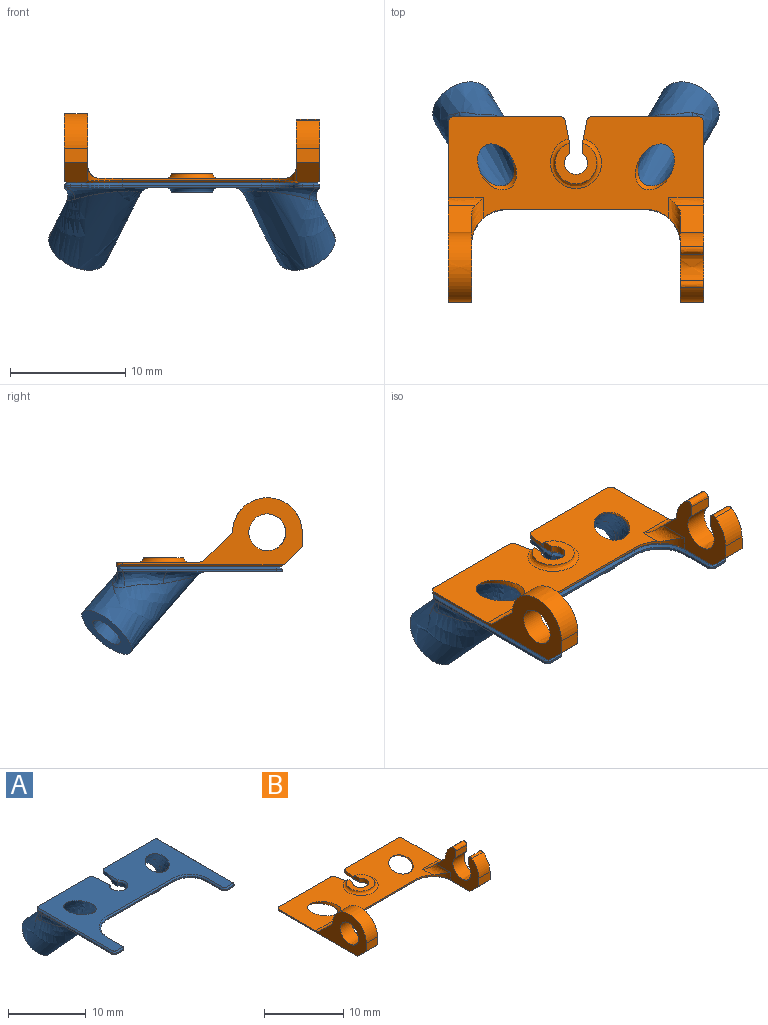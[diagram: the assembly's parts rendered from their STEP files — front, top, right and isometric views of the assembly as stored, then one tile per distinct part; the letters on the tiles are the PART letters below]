
ASSEMBLY  parts=2 mates=1
PART A: 60 faces, bbox 27.5x19.2x12.5 mm
  f0: plane 13.43x0.32mm, normal (1,0,0), area 2.7mm2, adj f16,f24,f33,f41,f59
  f1: plane 1.01x0.2mm, normal (0,-1,0), area 0.2mm2, adj f16,f24,f25,f57
  f2: plane 2.76x0.2mm, normal (-1,0,0), area 0.6mm2, adj f3,f16,f25,f55
  f3: cylinder r=3.01mm len=3.02mm, axis (0,0,1), area 0.9mm2, adj f2,f4,f16,f54
  f4: plane 12.06x0.2mm, normal (0,-1,0), area 2.4mm2, adj f3,f5,f16,f53
  f5: cylinder r=3.01mm len=3.02mm, axis (0,0,1), area 0.9mm2, adj f4,f6,f16,f52
  f6: plane 2.76x0.2mm, normal (1,0,0), area 0.6mm2, adj f5,f16,f26,f51
  f7: plane 1.01x0.2mm, normal (0,-1,0), area 0.2mm2, adj f16,f26,f27,f49
  f8: plane 13.43x0.33mm, normal (-1,0,0), area 2.7mm2, adj f16,f27,f28,f34,f47
  f9: plane 9.61x0.88mm, normal (0,1,0), area 3.7mm2, adj f16,f17,f28,f29,f37
  f10: plane 1.75x0.49mm, normal (0.98,0.19,0), area 0.6mm2, adj f16,f17,f29,f30,f43,f44
  f11: plane 0.98x0.63mm, normal (1,0,0), area 0.6mm2, adj f12,f30,f42,f43,f44
  f12: cylinder r=1.01mm len=2.01mm, axis (0,0,1), area 3.1mm2, adj f11,f13,f42,f45
  f13: plane 0.98x0.63mm, normal (-1,0,0), area 0.6mm2, adj f12,f31,f42,f43,f46
  f14: plane 1.75x0.49mm, normal (-0.98,0.19,0), area 0.6mm2, adj f16,f17,f31,f32,f43,f46
  f15: plane 9.6x0.87mm, normal (0,1,0), area 3.7mm2, adj f16,f17,f32,f33,f38
  f16: plane 22.29x14.5mm, normal (0,0,-1), area 90.3mm2, adj f0,f1,f2,f3,f4,f5,f6,f7
  f17: plane 21.71x14.11mm, normal (0,0,1), area 165mm2, adj f9,f10,f14,f15,f20,f23,f28,f29
  f18: plane 7.73x6.93mm, normal (0.35,0.61,-0.71), area 15.9mm2, adj f19,f20
  f19: extruded ~10.68x10.27mm, area 107.2mm2, adj f18,f38,f39,f40,f41
  f20: extruded ~8.84x8.23mm, area 76mm2, adj f17,f18
  f21: plane 7.73x6.93mm, normal (-0.35,0.61,-0.71), area 16.1mm2, adj f22,f23
  f22: extruded ~10.68x10.27mm, area 107.2mm2, adj f21,f34,f35,f36,f37
  f23: extruded ~8.84x8.23mm, area 76mm2, adj f17,f21
  f24: cylinder r=0.5mm len=0.5mm, axis (0,0,-1), area 0.2mm2, adj f0,f1,f16,f58
  f25: cylinder r=0.5mm len=0.5mm, axis (0,0,1), area 0.2mm2, adj f1,f2,f16,f56
  f26: cylinder r=0.5mm len=0.5mm, axis (0,0,-1), area 0.2mm2, adj f6,f7,f16,f50
  f27: cylinder r=0.5mm len=0.5mm, axis (0,0,1), area 0.2mm2, adj f7,f8,f16,f48
  f28: cylinder r=0.5mm len=0.5mm, axis (0,0,1), area 0.3mm2, adj f8,f9,f17,f36,f47
  f29: cylinder r=0.5mm len=0.49mm, axis (0,0,-1), area 0.3mm2, adj f9,f10,f16,f17
  f30: cylinder r=0.5mm len=0.4mm, axis (0,0,1), area 0mm2, adj f10,f11,f43,f44
  f31: cylinder r=0.5mm len=0.4mm, axis (0,0,1), area 0mm2, adj f13,f14,f43,f46
  f32: cylinder r=0.5mm len=0.49mm, axis (0,0,1), area 0.3mm2, adj f14,f15,f16,f17
  f33: cylinder r=0.5mm len=0.5mm, axis (0,0,-1), area 0.3mm2, adj f0,f15,f17,f40,f59
  f34: bspline ~3.99x1.35mm, area 4.7mm2, adj f8,f22,f35,f36
  f35: bspline ~7.75x7.5mm, area 16.4mm2, adj f16,f22,f34,f37
  f36: bspline ~1.43x1.06mm, area 1.4mm2, adj f22,f28,f34,f37
  f37: bspline ~5.39x1.22mm, area 3.9mm2, adj f9,f22,f35,f36
  f38: bspline ~5.39x1.22mm, area 3.9mm2, adj f15,f19,f39,f40
  f39: bspline ~7.75x7.5mm, area 16.4mm2, adj f16,f19,f38,f41
  f40: bspline ~1.43x1.06mm, area 1.4mm2, adj f19,f33,f38,f41
  f41: bspline ~3.99x1.35mm, area 4.7mm2, adj f0,f19,f39,f40
  f42: plane 3.62x3.52mm, normal (0,0,-1), area 6.1mm2, adj f11,f12,f13,f43
  f43: bspline ~4.39x4.26mm, area 7mm2, adj f10,f11,f13,f14,f16,f30,f31,f42
  f44: plane 2.03x0.21mm, normal (0.71,0,0.71), area 0.4mm2, adj f10,f11,f17,f30,f45
  f45: cone r=1.01mm half-angle=45deg, axis (0,0,1), area 1.6mm2, adj f12,f17,f44,f46
  f46: plane 2.03x0.21mm, normal (-0.71,0,0.71), area 0.4mm2, adj f13,f14,f17,f31,f45
  f47: plane 13.8x0.29mm, normal (-0.71,0,0.71), area 3.8mm2, adj f8,f17,f28,f48
  f48: cone r=0.3mm half-angle=45deg, axis (0,0,-1), area 0.2mm2, adj f17,f27,f47,f49
  f49: plane 1.01x0.2mm, normal (0,-0.71,0.71), area 0.3mm2, adj f7,f17,f48,f50
  f50: cone r=0.3mm half-angle=45deg, axis (0,0,-1), area 0.2mm2, adj f17,f26,f49,f51
  f51: plane 2.76x0.2mm, normal (0.71,0,0.71), area 0.8mm2, adj f6,f17,f50,f52
  f52: cone r=3.01mm half-angle=45deg, axis (0,0,1), area 1.4mm2, adj f5,f17,f51,f53
  f53: plane 12.06x0.2mm, normal (0,-0.71,0.71), area 3.4mm2, adj f4,f17,f52,f54
  f54: cone r=3.01mm half-angle=45deg, axis (0,0,1), area 1.4mm2, adj f3,f17,f53,f55
  f55: plane 2.76x0.2mm, normal (-0.71,0,0.71), area 0.8mm2, adj f2,f17,f54,f56
  f56: cone r=0.3mm half-angle=45deg, axis (0,0,-1), area 0.2mm2, adj f17,f25,f55,f57
  f57: plane 1.01x0.2mm, normal (0,-0.71,0.71), area 0.3mm2, adj f1,f17,f56,f58
  f58: cone r=0.3mm half-angle=45deg, axis (0,0,-1), area 0.2mm2, adj f17,f24,f57,f59
  f59: plane 13.8x0.29mm, normal (0.71,0,0.71), area 3.8mm2, adj f0,f17,f33,f58
PART B: 55 faces, bbox 23.8x17.8x10.7 mm
  f0: plane 22.11x8.81mm, normal (0,0,1), area 133.7mm2, adj f1,f5,f9,f10,f11,f12,f13,f29
  f1: plane 16.15x5.92mm, normal (1,0,0), area 23.6mm2, adj f0,f3,f4,f21,f22,f23,f24,f25
  f2: plane 8.21x5.92mm, normal (-1,0,0), area 18.3mm2, adj f3,f4,f21,f22,f23,f24,f25,f26
  f3: extruded ~2.42x2.01mm, area 5.7mm2, adj f1,f2,f21,f27
  f4: extruded ~3.21x2.73mm, area 15.2mm2, adj f1,f2,f25,f26
  f5: plane 12.06x0.2mm, normal (0,-1,0), area 2.4mm2, adj f0,f29,f30,f52
  f6: plane 0.98x0.63mm, normal (-1,0,0), area 0.6mm2, adj f7,f42,f43,f44,f45
  f7: cylinder r=1.01mm len=2.01mm, axis (0,0,-1), area 3.1mm2, adj f6,f8,f43,f46
  f8: plane 0.98x0.63mm, normal (1,0,0), area 0.6mm2, adj f7,f37,f43,f44,f47
  f9: plane 1.75x0.49mm, normal (0.98,0.19,0), area 0.6mm2, adj f0,f14,f37,f38,f44,f47
  f10: plane 9.13x0.4mm, normal (0,1,0), area 3.7mm2, adj f0,f14,f38,f39
  f11: plane 17.26x8.39mm, normal (-1,0,0), area 27mm2, adj f0,f16,f17,f18,f19,f20,f34,f39
  f12: plane 9.13x0.4mm, normal (0,1,0), area 3.7mm2, adj f0,f14,f40,f41
  f13: plane 1.75x0.49mm, normal (-0.98,0.19,0), area 0.6mm2, adj f0,f14,f41,f42,f44,f45
  f14: plane 21.71x14.31mm, normal (0,0,-1), area 165.7mm2, adj f9,f10,f12,f13,f19,f24,f35,f36
  f15: plane 9.32x8.39mm, normal (1,0,0), area 21.9mm2, adj f16,f17,f18,f19,f20,f30,f33,f54
  f16: plane 2.39x2.38mm, normal (0,0.71,0.71), area 6.7mm2, adj f11,f15,f17,f33,f34
  f17: extruded ~6.03x3mm, area 19mm2, adj f11,f15,f16,f18
  f18: plane 2.01x1.24mm, normal (0,-1,0), area 2.5mm2, adj f11,f15,f17,f19
  f19: plane 2.01x1.77mm, normal (0,-0.71,-0.71), area 5mm2, adj f11,f14,f15,f18,f49,f54
  f20: extruded ~3.22x3.2mm, area 20.3mm2, adj f11,f15
  f21: plane 2.39x2.38mm, normal (0,0.71,0.71), area 6.7mm2, adj f1,f2,f3,f31,f32
  f22: extruded ~2.42x2.01mm, area 5.7mm2, adj f1,f2,f23,f28
  f23: plane 2.01x1.24mm, normal (0,-1,0), area 2.5mm2, adj f1,f2,f22,f24
  f24: plane 2.01x1.77mm, normal (0,-0.71,-0.71), area 5mm2, adj f1,f2,f14,f23,f48,f50
  f25: plane 2.01x0.97mm, normal (0,1,0), area 1.9mm2, adj f1,f2,f4,f28
  f26: plane 2.01x0.97mm, normal (0,-1,0), area 1.9mm2, adj f1,f2,f4,f27
  f27: extruded ~2.01x0.64mm, area 1.8mm2, adj f1,f2,f3,f26
  f28: extruded ~2.01x0.64mm, area 1.8mm2, adj f1,f2,f22,f25
  f29: cylinder r=3.01mm len=3.02mm, axis (0,0,1), area 1.9mm2, adj f0,f2,f5,f31,f51
  f30: cylinder r=3.01mm len=3.02mm, axis (0,0,-1), area 1.9mm2, adj f0,f5,f15,f33,f53
  f31: extruded ~4.03x1.01mm, area 3.6mm2, adj f0,f2,f21,f29,f32
  f32: extruded ~3.02x0.71mm, area 2.1mm2, adj f0,f1,f21,f31
  f33: extruded ~4.03x1.01mm, area 3.6mm2, adj f0,f15,f16,f30,f34
  f34: extruded ~3.02x0.71mm, area 2.1mm2, adj f0,f11,f16,f33
  f35: extruded ~4.65x4.58mm, area 5.4mm2, adj f0,f14
  f36: extruded ~4.65x4.58mm, area 5.4mm2, adj f0,f14
  f37: cylinder r=0.5mm len=0.4mm, axis (0,0,-1), area 0mm2, adj f8,f9,f44,f47
  f38: cylinder r=0.5mm len=0.49mm, axis (0,0,1), area 0.3mm2, adj f0,f9,f10,f14
  f39: cylinder r=0.5mm len=0.5mm, axis (0,0,-1), area 0.3mm2, adj f0,f10,f11,f14,f49
  f40: cylinder r=0.5mm len=0.5mm, axis (0,0,1), area 0.3mm2, adj f0,f1,f12,f14,f48
  f41: cylinder r=0.5mm len=0.49mm, axis (0,0,-1), area 0.3mm2, adj f0,f12,f13,f14
  f42: cylinder r=0.5mm len=0.4mm, axis (0,0,-1), area 0mm2, adj f6,f13,f44,f45
  f43: plane 3.62x3.52mm, normal (0,0,1), area 6.1mm2, adj f6,f7,f8,f44
  f44: bspline ~4.39x4.26mm, area 7mm2, adj f0,f6,f8,f9,f13,f37,f42,f43
  f45: plane 2.03x0.21mm, normal (-0.71,0,-0.71), area 0.4mm2, adj f6,f13,f14,f42,f46
  f46: cone r=1.2mm half-angle=45deg, axis (0,0,-1), area 1.6mm2, adj f7,f14,f45,f47
  f47: plane 2.03x0.21mm, normal (0.71,0,-0.71), area 0.4mm2, adj f8,f9,f14,f37,f46
  f48: plane 14.51x0.29mm, normal (0.71,0,-0.71), area 4mm2, adj f1,f14,f24,f40
  f49: plane 14.51x0.29mm, normal (-0.71,0,-0.71), area 4mm2, adj f11,f14,f19,f39
  f50: plane 3.46x0.2mm, normal (-0.71,0,-0.71), area 1mm2, adj f2,f14,f24,f51
  f51: cone r=3.21mm half-angle=45deg, axis (0,0,-1), area 1.4mm2, adj f14,f29,f50,f52
  f52: plane 12.06x0.2mm, normal (0,-0.71,-0.71), area 3.4mm2, adj f5,f14,f51,f53
  f53: cone r=3.21mm half-angle=45deg, axis (0,0,-1), area 1.4mm2, adj f14,f30,f52,f54
  f54: plane 3.46x0.2mm, normal (0.71,0,-0.71), area 1mm2, adj f14,f15,f19,f53
PLACE A t=(-2.56,-1.96,6.99)mm
PLACE B t=(-2.56,-1.92,6.99)mm fixed
MATE fastened B.f14 <-> A.f17  axis (0,0,-1) through (-2.56,6.11,6.99)mm
